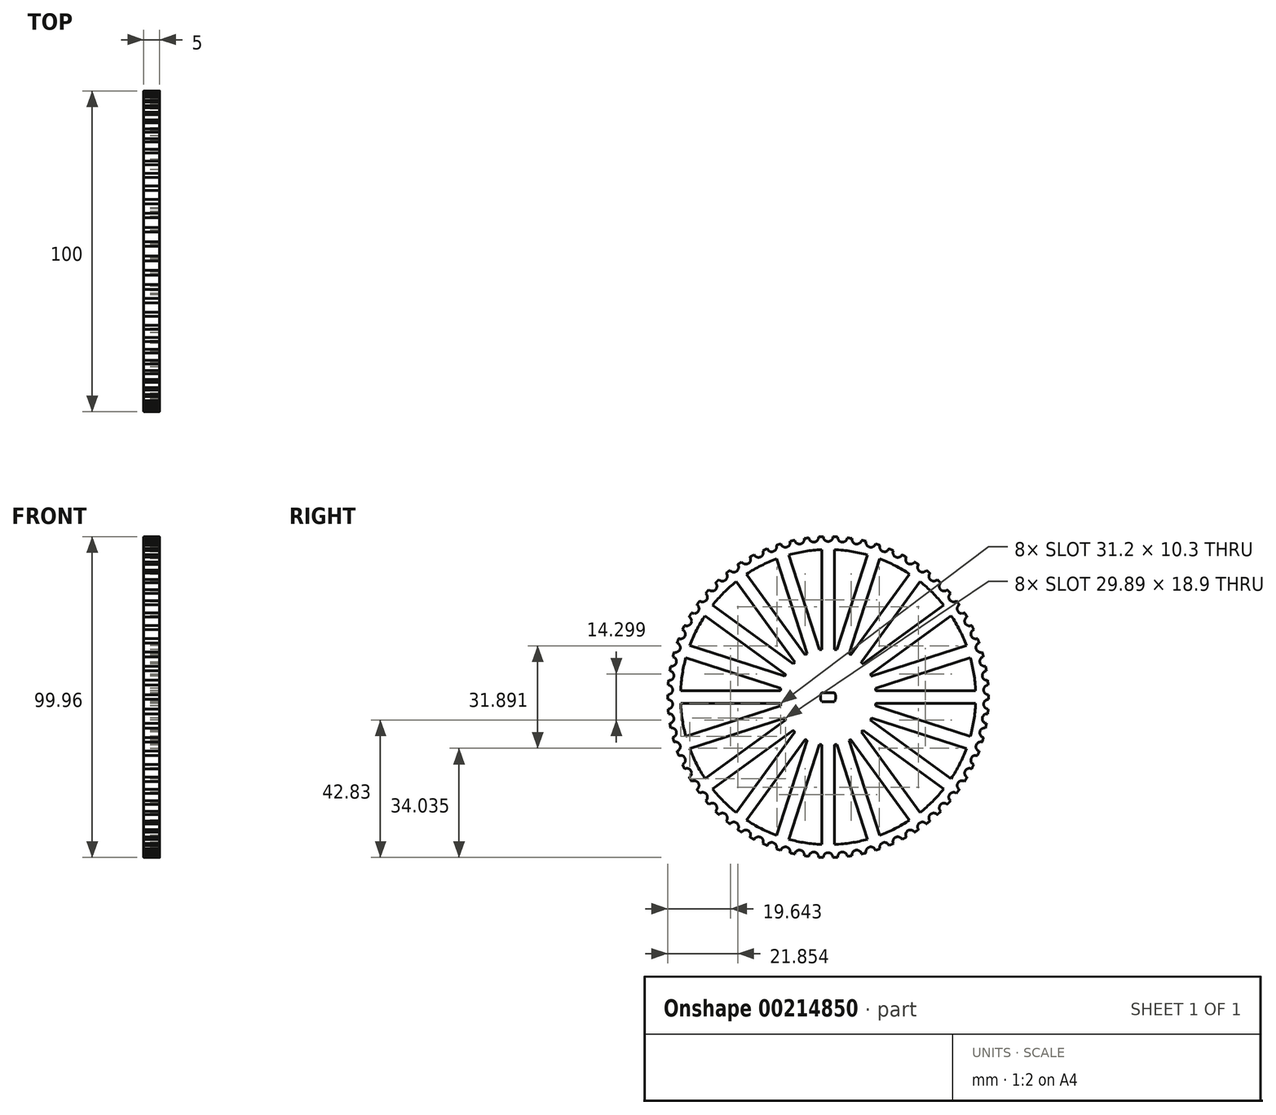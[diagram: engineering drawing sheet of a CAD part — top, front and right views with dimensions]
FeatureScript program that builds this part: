
annotation { "Feature Type Name" : "Feature", "Feature Type Description" : "" }
export const myFeature = defineFeature(function(context is Context, id is Id, definition is map)
    precondition{}
    {
        {
            var Q0;
            Q0=qCreatedBy(makeId("Top.planeOp"),FACE);
            var sketch = newSketch(context, id + "F0", { "sketchPlane" : qUnion([Q0])});
            skLineSegment(sketch, "E0.bottom", {"start": v(-40, 60) * mm, "end": v(40, 60) * mm});
            skLineSegment(sketch, "E0.top", {"start": v(-40, -60) * mm, "end": v(40, -60) * mm});
            skLineSegment(sketch, "E0.left", {"start": v(-40, 60) * mm, "end": v(-40, -60) * mm});
            skLineSegment(sketch, "E0.right", {"start": v(40, 60) * mm, "end": v(40, -60) * mm});
            skPoint(sketch, "E0.middle", {"position": v(0, 0) * mm});
            skSolve(sketch);
        }
        {
            var Q0;
            Q0=sQuery(id+"F0.wireOp",EDGE,"E0.left");
            cPlane(context, id + "F1", {"entities" : qUnion([Q0]), "cplaneType" : CPlaneType.LINE_ANGLE, "offset" : 25 * mm, "angle" : 90 * degree, "width" : 150 * mm, "height" : 150 * mm});
        }
        {
            var Q0;
            Q0=qCreatedBy(id+"F1.planeOp",FACE);
            var sketch = newSketch(context, id + "F2", { "sketchPlane" : qUnion([Q0])});
            skCircle(sketch, "E1", {"center": v(0, 0) * mm, "radius": 50 * mm});
            skCircle(sketch, "E2", {"center": v(0, 0) * mm, "radius": 46 * mm});
            skCircle(sketch, "E3", {"center": v(0, 0) * mm, "radius": 2 * mm});
            skLineSegment(sketch, "E4", {"start": v(0, 2) * mm, "end": v(45.96, 2) * mm});
            skLineSegment(sketch, "E5", {"start": v(0, -2) * mm, "end": v(45.96, -2) * mm});
            skLineSegment(sketch, "E6.1.0", {"start": v(-0.62, 1.9) * mm, "end": v(43.09, 16.1) * mm});
            skLineSegment(sketch, "E6.1.1", {"start": v(0.62, -1.9) * mm, "end": v(44.33, 12.3) * mm});
            skLineSegment(sketch, "E6.2.0", {"start": v(-1.18, 1.62) * mm, "end": v(36, 28.63) * mm});
            skLineSegment(sketch, "E6.2.1", {"start": v(1.18, -1.62) * mm, "end": v(38.36, 25.4) * mm});
            skLineSegment(sketch, "E6.3.0", {"start": v(-1.62, 1.18) * mm, "end": v(25.4, 38.36) * mm});
            skLineSegment(sketch, "E6.3.1", {"start": v(1.62, -1.18) * mm, "end": v(28.63, 36) * mm});
            skLineSegment(sketch, "E6.4.0", {"start": v(-1.9, 0.62) * mm, "end": v(12.3, 44.33) * mm});
            skLineSegment(sketch, "E6.4.1", {"start": v(1.9, -0.62) * mm, "end": v(16.1, 43.09) * mm});
            skLineSegment(sketch, "E6.5.0", {"start": v(-2, 0) * mm, "end": v(-2, 45.96) * mm});
            skLineSegment(sketch, "E6.5.1", {"start": v(2, 0) * mm, "end": v(2, 45.96) * mm});
            skLineSegment(sketch, "E6.6.0", {"start": v(-1.9, -0.62) * mm, "end": v(-16.1, 43.09) * mm});
            skLineSegment(sketch, "E6.6.1", {"start": v(1.9, 0.62) * mm, "end": v(-12.3, 44.33) * mm});
            skLineSegment(sketch, "E6.7.0", {"start": v(-1.62, -1.18) * mm, "end": v(-28.63, 36) * mm});
            skLineSegment(sketch, "E6.7.1", {"start": v(1.62, 1.18) * mm, "end": v(-25.4, 38.36) * mm});
            skLineSegment(sketch, "E6.8.0", {"start": v(-1.18, -1.62) * mm, "end": v(-38.36, 25.4) * mm});
            skLineSegment(sketch, "E6.8.1", {"start": v(1.18, 1.62) * mm, "end": v(-36, 28.63) * mm});
            skLineSegment(sketch, "E6.9.0", {"start": v(-0.62, -1.9) * mm, "end": v(-44.33, 12.3) * mm});
            skLineSegment(sketch, "E6.9.1", {"start": v(0.62, 1.9) * mm, "end": v(-43.09, 16.1) * mm});
            skLineSegment(sketch, "E6.10.0", {"start": v(0, -2) * mm, "end": v(-45.96, -2) * mm});
            skLineSegment(sketch, "E6.10.1", {"start": v(0, 2) * mm, "end": v(-45.96, 2) * mm});
            skLineSegment(sketch, "E6.11.0", {"start": v(0.62, -1.9) * mm, "end": v(-43.09, -16.1) * mm});
            skLineSegment(sketch, "E6.11.1", {"start": v(-0.62, 1.9) * mm, "end": v(-44.33, -12.3) * mm});
            skLineSegment(sketch, "E6.12.0", {"start": v(1.18, -1.62) * mm, "end": v(-36, -28.63) * mm});
            skLineSegment(sketch, "E6.12.1", {"start": v(-1.18, 1.62) * mm, "end": v(-38.36, -25.4) * mm});
            skLineSegment(sketch, "E6.13.0", {"start": v(1.62, -1.18) * mm, "end": v(-25.4, -38.36) * mm});
            skLineSegment(sketch, "E6.13.1", {"start": v(-1.62, 1.18) * mm, "end": v(-28.63, -36) * mm});
            skLineSegment(sketch, "E6.14.0", {"start": v(1.9, -0.62) * mm, "end": v(-12.3, -44.33) * mm});
            skLineSegment(sketch, "E6.14.1", {"start": v(-1.9, 0.62) * mm, "end": v(-16.1, -43.09) * mm});
            skLineSegment(sketch, "E6.15.0", {"start": v(2, 0) * mm, "end": v(2, -45.96) * mm});
            skLineSegment(sketch, "E6.15.1", {"start": v(-2, 0) * mm, "end": v(-2, -45.96) * mm});
            skLineSegment(sketch, "E6.16.0", {"start": v(1.9, 0.62) * mm, "end": v(16.1, -43.09) * mm});
            skLineSegment(sketch, "E6.16.1", {"start": v(-1.9, -0.62) * mm, "end": v(12.3, -44.33) * mm});
            skLineSegment(sketch, "E6.17.0", {"start": v(1.62, 1.18) * mm, "end": v(28.63, -36) * mm});
            skLineSegment(sketch, "E6.17.1", {"start": v(-1.62, -1.18) * mm, "end": v(25.4, -38.36) * mm});
            skLineSegment(sketch, "E6.18.0", {"start": v(1.18, 1.62) * mm, "end": v(38.36, -25.4) * mm});
            skLineSegment(sketch, "E6.18.1", {"start": v(-1.18, -1.62) * mm, "end": v(36, -28.63) * mm});
            skLineSegment(sketch, "E6.19.0", {"start": v(0.62, 1.9) * mm, "end": v(44.33, -12.3) * mm});
            skLineSegment(sketch, "E6.19.1", {"start": v(-0.62, -1.9) * mm, "end": v(43.09, -16.1) * mm});
            skCircle(sketch, "E7", {"center": v(0, 0) * mm, "radius": 12.5 * mm, "construction": true});
            skCircle(sketch, "E8", {"center": v(0, 0) * mm, "radius": 14 * mm});
            skCircle(sketch, "E9", {"center": v(0, 50) * mm, "radius": 1.5 * mm});
            skCircle(sketch, "E10.1.0", {"center": v(-4.48, 49.8) * mm, "radius": 1.5 * mm});
            skCircle(sketch, "E10.2.0", {"center": v(-8.93, 49.2) * mm, "radius": 1.5 * mm});
            skCircle(sketch, "E10.3.0", {"center": v(-13.3, 48.2) * mm, "radius": 1.5 * mm});
            skCircle(sketch, "E10.4.0", {"center": v(-17.57, 46.81) * mm, "radius": 1.5 * mm});
            skCircle(sketch, "E10.5.0", {"center": v(-21.7, 45.05) * mm, "radius": 1.5 * mm});
            skCircle(sketch, "E10.6.0", {"center": v(-25.64, 42.92) * mm, "radius": 1.5 * mm});
            skCircle(sketch, "E10.7.0", {"center": v(-29.39, 40.45) * mm, "radius": 1.5 * mm});
            skCircle(sketch, "E10.8.0", {"center": v(-32.9, 37.65) * mm, "radius": 1.5 * mm});
            skCircle(sketch, "E10.9.0", {"center": v(-36.14, 34.55) * mm, "radius": 1.5 * mm});
            skCircle(sketch, "E10.10.0", {"center": v(-39.1, 31.17) * mm, "radius": 1.5 * mm});
            skCircle(sketch, "E10.11.0", {"center": v(-41.73, 27.54) * mm, "radius": 1.5 * mm});
            skCircle(sketch, "E10.12.0", {"center": v(-44.03, 23.7) * mm, "radius": 1.5 * mm});
            skCircle(sketch, "E10.13.0", {"center": v(-45.98, 19.65) * mm, "radius": 1.5 * mm});
            skCircle(sketch, "E10.14.0", {"center": v(-47.55, 15.45) * mm, "radius": 1.5 * mm});
            skCircle(sketch, "E10.15.0", {"center": v(-48.75, 11.13) * mm, "radius": 1.5 * mm});
            skCircle(sketch, "E10.16.0", {"center": v(-49.55, 6.71) * mm, "radius": 1.5 * mm});
            skCircle(sketch, "E10.17.0", {"center": v(-49.95, 2.24) * mm, "radius": 1.5 * mm});
            skCircle(sketch, "E10.18.0", {"center": v(-49.95, -2.24) * mm, "radius": 1.5 * mm});
            skCircle(sketch, "E10.19.0", {"center": v(-49.55, -6.71) * mm, "radius": 1.5 * mm});
            skCircle(sketch, "E10.20.0", {"center": v(-48.75, -11.13) * mm, "radius": 1.5 * mm});
            skCircle(sketch, "E10.21.0", {"center": v(-47.55, -15.45) * mm, "radius": 1.5 * mm});
            skCircle(sketch, "E10.22.0", {"center": v(-45.98, -19.65) * mm, "radius": 1.5 * mm});
            skCircle(sketch, "E10.23.0", {"center": v(-44.03, -23.7) * mm, "radius": 1.5 * mm});
            skCircle(sketch, "E10.24.0", {"center": v(-41.73, -27.54) * mm, "radius": 1.5 * mm});
            skCircle(sketch, "E10.25.0", {"center": v(-39.1, -31.17) * mm, "radius": 1.5 * mm});
            skCircle(sketch, "E10.26.0", {"center": v(-36.14, -34.55) * mm, "radius": 1.5 * mm});
            skCircle(sketch, "E10.27.0", {"center": v(-32.9, -37.65) * mm, "radius": 1.5 * mm});
            skCircle(sketch, "E10.28.0", {"center": v(-29.39, -40.45) * mm, "radius": 1.5 * mm});
            skCircle(sketch, "E10.29.0", {"center": v(-25.64, -42.92) * mm, "radius": 1.5 * mm});
            skCircle(sketch, "E10.30.0", {"center": v(-21.7, -45.05) * mm, "radius": 1.5 * mm});
            skCircle(sketch, "E10.31.0", {"center": v(-17.57, -46.81) * mm, "radius": 1.5 * mm});
            skCircle(sketch, "E10.32.0", {"center": v(-13.3, -48.2) * mm, "radius": 1.5 * mm});
            skCircle(sketch, "E10.33.0", {"center": v(-8.93, -49.2) * mm, "radius": 1.5 * mm});
            skCircle(sketch, "E10.34.0", {"center": v(-4.48, -49.8) * mm, "radius": 1.5 * mm});
            skCircle(sketch, "E10.35.0", {"center": v(0, -50) * mm, "radius": 1.5 * mm});
            skCircle(sketch, "E10.36.0", {"center": v(4.48, -49.8) * mm, "radius": 1.5 * mm});
            skCircle(sketch, "E10.37.0", {"center": v(8.93, -49.2) * mm, "radius": 1.5 * mm});
            skCircle(sketch, "E10.38.0", {"center": v(13.3, -48.2) * mm, "radius": 1.5 * mm});
            skCircle(sketch, "E10.39.0", {"center": v(17.57, -46.81) * mm, "radius": 1.5 * mm});
            skCircle(sketch, "E10.40.0", {"center": v(21.7, -45.05) * mm, "radius": 1.5 * mm});
            skCircle(sketch, "E10.41.0", {"center": v(25.64, -42.92) * mm, "radius": 1.5 * mm});
            skCircle(sketch, "E10.42.0", {"center": v(29.39, -40.45) * mm, "radius": 1.5 * mm});
            skCircle(sketch, "E10.43.0", {"center": v(32.9, -37.65) * mm, "radius": 1.5 * mm});
            skCircle(sketch, "E10.44.0", {"center": v(36.14, -34.55) * mm, "radius": 1.5 * mm});
            skCircle(sketch, "E10.45.0", {"center": v(39.1, -31.17) * mm, "radius": 1.5 * mm});
            skCircle(sketch, "E10.46.0", {"center": v(41.73, -27.54) * mm, "radius": 1.5 * mm});
            skCircle(sketch, "E10.47.0", {"center": v(44.03, -23.7) * mm, "radius": 1.5 * mm});
            skCircle(sketch, "E10.48.0", {"center": v(45.98, -19.65) * mm, "radius": 1.5 * mm});
            skCircle(sketch, "E10.49.0", {"center": v(47.55, -15.45) * mm, "radius": 1.5 * mm});
            skCircle(sketch, "E10.50.0", {"center": v(48.75, -11.13) * mm, "radius": 1.5 * mm});
            skCircle(sketch, "E10.51.0", {"center": v(49.55, -6.71) * mm, "radius": 1.5 * mm});
            skCircle(sketch, "E10.52.0", {"center": v(49.95, -2.24) * mm, "radius": 1.5 * mm});
            skCircle(sketch, "E10.53.0", {"center": v(49.95, 2.24) * mm, "radius": 1.5 * mm});
            skCircle(sketch, "E10.54.0", {"center": v(49.55, 6.71) * mm, "radius": 1.5 * mm});
            skCircle(sketch, "E10.55.0", {"center": v(48.75, 11.13) * mm, "radius": 1.5 * mm});
            skCircle(sketch, "E10.56.0", {"center": v(47.55, 15.45) * mm, "radius": 1.5 * mm});
            skCircle(sketch, "E10.57.0", {"center": v(45.98, 19.65) * mm, "radius": 1.5 * mm});
            skCircle(sketch, "E10.58.0", {"center": v(44.03, 23.7) * mm, "radius": 1.5 * mm});
            skCircle(sketch, "E10.59.0", {"center": v(41.73, 27.54) * mm, "radius": 1.5 * mm});
            skCircle(sketch, "E10.60.0", {"center": v(39.1, 31.17) * mm, "radius": 1.5 * mm});
            skCircle(sketch, "E10.61.0", {"center": v(36.14, 34.55) * mm, "radius": 1.5 * mm});
            skCircle(sketch, "E10.62.0", {"center": v(32.9, 37.65) * mm, "radius": 1.5 * mm});
            skCircle(sketch, "E10.63.0", {"center": v(29.39, 40.45) * mm, "radius": 1.5 * mm});
            skCircle(sketch, "E10.64.0", {"center": v(25.64, 42.92) * mm, "radius": 1.5 * mm});
            skCircle(sketch, "E10.65.0", {"center": v(21.7, 45.05) * mm, "radius": 1.5 * mm});
            skCircle(sketch, "E10.66.0", {"center": v(17.57, 46.81) * mm, "radius": 1.5 * mm});
            skCircle(sketch, "E10.67.0", {"center": v(13.3, 48.2) * mm, "radius": 1.5 * mm});
            skCircle(sketch, "E10.68.0", {"center": v(8.93, 49.2) * mm, "radius": 1.5 * mm});
            skCircle(sketch, "E10.69.0", {"center": v(4.48, 49.8) * mm, "radius": 1.5 * mm});
            skSolve(sketch);
        }
        {
            var Q0;
            Q0=qCreatedBy(id+"F1.planeOp",FACE);
            var sketch = newSketch(context, id + "F3", { "sketchPlane" : qUnion([Q0])});
            skCircle(sketch, "E11", {"center": v(0, 0) * mm, "radius": 15 * mm});
            skCircle(sketch, "E12.0", {"center": v(0, 0) * mm, "radius": 46 * mm});
            skCircle(sketch, "E13.0", {"center": v(0, 0) * mm, "radius": 50 * mm});
            skCircle(sketch, "E14", {"center": v(0, 0) * mm, "radius": 2.4 * mm});
            skLineSegment(sketch, "E15", {"start": v(1.95, 1.4) * mm, "end": v(-1.95, 1.4) * mm});
            skLineSegment(sketch, "E16.MirrorCS", {"start": v(1.95, -1.4) * mm, "end": v(-1.95, -1.4) * mm});
            skSolve(sketch);
        }
        {
            var Q0;
            Q0=makeQuery(id+"F3.imprint","IMPRINT",FACE,{"disambiguationData":[TD([[makeQuery(id+"F3.imprint","IMPRINT",EDGE,{"derivedFrom":sQuery(id+"F3.wireOp",EDGE,"E11")}),1.0]])]});
            var Q1;
            {var subQ0=sQuery(id+"F3.wireOp",EDGE,"E15");Q1=makeQuery(id+"F3.imprint","IMPRINT",FACE,{"disambiguationData":[TD([[makeQuery(id+"F3.imprint","IMPRINT",EDGE,{"derivedFrom":subQ0}),-1.0]])]});}
            var Q2;
            {var subQ0=sQuery(id+"F3.wireOp",EDGE,"E16.MirrorCS");Q2=makeQuery(id+"F3.imprint","IMPRINT",FACE,{"disambiguationData":[TD([[makeQuery(id+"F3.imprint","IMPRINT",EDGE,{"derivedFrom":subQ0}),1.0]])]});}
            extrude(context, id + "F4", {"entities" : qUnion([Q0, Q1, Q2]), "depth" : 5 * mm});
        }
        {
            var Q0;
            {var subQ0=sQuery(id+"F2.wireOp",EDGE,"E6.3.0");var subQ1=sQuery(id+"F2.wireOp",EDGE,"E2");var subQ2=makeQuery(id+"F2.imprint","INTERSECT",VERTEX,{"derivedFrom":[subQ1,subQ0]});Q0=makeQuery(id+"F2.imprint","IMPRINT",FACE,{"disambiguationData":[TD([[makeQuery(id+"F2.imprint","IMPRINT",EDGE,{"disambiguationData":[TD([[subQ2,1.0]])],"derivedFrom":subQ1}),1.0]])]});}
            var Q1;
            {var subQ0=sQuery(id+"F2.wireOp",EDGE,"E6.2.0");var subQ1=sQuery(id+"F2.wireOp",EDGE,"E2");var subQ2=makeQuery(id+"F2.imprint","INTERSECT",VERTEX,{"derivedFrom":[subQ1,subQ0]});Q1=makeQuery(id+"F2.imprint","IMPRINT",FACE,{"disambiguationData":[TD([[makeQuery(id+"F2.imprint","IMPRINT",EDGE,{"disambiguationData":[TD([[subQ2,1.0]])],"derivedFrom":subQ1}),1.0]])]});}
            var Q2;
            {var subQ0=sQuery(id+"F2.wireOp",EDGE,"E6.1.0");var subQ1=sQuery(id+"F2.wireOp",EDGE,"E2");var subQ2=makeQuery(id+"F2.imprint","INTERSECT",VERTEX,{"derivedFrom":[subQ1,subQ0]});Q2=makeQuery(id+"F2.imprint","IMPRINT",FACE,{"disambiguationData":[TD([[makeQuery(id+"F2.imprint","IMPRINT",EDGE,{"disambiguationData":[TD([[subQ2,1.0]])],"derivedFrom":subQ1}),1.0]])]});}
            var Q3;
            {var subQ0=sQuery(id+"F2.wireOp",EDGE,"E4");var subQ1=sQuery(id+"F2.wireOp",EDGE,"E2");var subQ2=makeQuery(id+"F2.imprint","INTERSECT",VERTEX,{"derivedFrom":[subQ1,subQ0]});Q3=makeQuery(id+"F2.imprint","IMPRINT",FACE,{"disambiguationData":[TD([[makeQuery(id+"F2.imprint","IMPRINT",EDGE,{"disambiguationData":[TD([[subQ2,1.0]])],"derivedFrom":subQ1}),1.0]])]});}
            var Q4;
            {var subQ0=sQuery(id+"F2.wireOp",EDGE,"E6.19.0");var subQ1=sQuery(id+"F2.wireOp",EDGE,"E2");var subQ2=makeQuery(id+"F2.imprint","INTERSECT",VERTEX,{"derivedFrom":[subQ1,subQ0]});Q4=makeQuery(id+"F2.imprint","IMPRINT",FACE,{"disambiguationData":[TD([[makeQuery(id+"F2.imprint","IMPRINT",EDGE,{"disambiguationData":[TD([[subQ2,1.0]])],"derivedFrom":subQ1}),1.0]])]});}
            var Q5;
            {var subQ0=sQuery(id+"F2.wireOp",EDGE,"E6.18.0");var subQ1=sQuery(id+"F2.wireOp",EDGE,"E2");var subQ2=makeQuery(id+"F2.imprint","INTERSECT",VERTEX,{"derivedFrom":[subQ1,subQ0]});Q5=makeQuery(id+"F2.imprint","IMPRINT",FACE,{"disambiguationData":[TD([[makeQuery(id+"F2.imprint","IMPRINT",EDGE,{"disambiguationData":[TD([[subQ2,1.0]])],"derivedFrom":subQ1}),1.0]])]});}
            var Q6;
            {var subQ0=sQuery(id+"F2.wireOp",EDGE,"E6.17.0");var subQ1=sQuery(id+"F2.wireOp",EDGE,"E2");var subQ2=makeQuery(id+"F2.imprint","INTERSECT",VERTEX,{"derivedFrom":[subQ1,subQ0]});Q6=makeQuery(id+"F2.imprint","IMPRINT",FACE,{"disambiguationData":[TD([[makeQuery(id+"F2.imprint","IMPRINT",EDGE,{"disambiguationData":[TD([[subQ2,1.0]])],"derivedFrom":subQ1}),1.0]])]});}
            var Q7;
            {var subQ0=sQuery(id+"F2.wireOp",EDGE,"E6.16.0");var subQ1=sQuery(id+"F2.wireOp",EDGE,"E2");var subQ2=makeQuery(id+"F2.imprint","INTERSECT",VERTEX,{"derivedFrom":[subQ1,subQ0]});Q7=makeQuery(id+"F2.imprint","IMPRINT",FACE,{"disambiguationData":[TD([[makeQuery(id+"F2.imprint","IMPRINT",EDGE,{"disambiguationData":[TD([[subQ2,1.0]])],"derivedFrom":subQ1}),1.0]])]});}
            var Q8;
            {var subQ0=sQuery(id+"F2.wireOp",EDGE,"E6.15.0");var subQ1=sQuery(id+"F2.wireOp",EDGE,"E2");var subQ2=makeQuery(id+"F2.imprint","INTERSECT",VERTEX,{"derivedFrom":[subQ1,subQ0]});Q8=makeQuery(id+"F2.imprint","IMPRINT",FACE,{"disambiguationData":[TD([[makeQuery(id+"F2.imprint","IMPRINT",EDGE,{"disambiguationData":[TD([[subQ2,1.0]])],"derivedFrom":subQ1}),1.0]])]});}
            var Q9;
            {var subQ0=sQuery(id+"F2.wireOp",EDGE,"E6.14.0");var subQ1=sQuery(id+"F2.wireOp",EDGE,"E2");var subQ2=makeQuery(id+"F2.imprint","INTERSECT",VERTEX,{"derivedFrom":[subQ1,subQ0]});Q9=makeQuery(id+"F2.imprint","IMPRINT",FACE,{"disambiguationData":[TD([[makeQuery(id+"F2.imprint","IMPRINT",EDGE,{"disambiguationData":[TD([[subQ2,1.0]])],"derivedFrom":subQ1}),1.0]])]});}
            var Q10;
            {var subQ0=sQuery(id+"F2.wireOp",EDGE,"E6.13.0");var subQ1=sQuery(id+"F2.wireOp",EDGE,"E2");var subQ2=makeQuery(id+"F2.imprint","INTERSECT",VERTEX,{"derivedFrom":[subQ1,subQ0]});Q10=makeQuery(id+"F2.imprint","IMPRINT",FACE,{"disambiguationData":[TD([[makeQuery(id+"F2.imprint","IMPRINT",EDGE,{"disambiguationData":[TD([[subQ2,1.0]])],"derivedFrom":subQ1}),1.0]])]});}
            var Q11;
            {var subQ0=sQuery(id+"F2.wireOp",EDGE,"E6.12.0");var subQ1=sQuery(id+"F2.wireOp",EDGE,"E2");var subQ2=makeQuery(id+"F2.imprint","INTERSECT",VERTEX,{"derivedFrom":[subQ1,subQ0]});Q11=makeQuery(id+"F2.imprint","IMPRINT",FACE,{"disambiguationData":[TD([[makeQuery(id+"F2.imprint","IMPRINT",EDGE,{"disambiguationData":[TD([[subQ2,1.0]])],"derivedFrom":subQ1}),1.0]])]});}
            var Q12;
            {var subQ0=sQuery(id+"F2.wireOp",EDGE,"E6.11.0");var subQ1=sQuery(id+"F2.wireOp",EDGE,"E2");var subQ2=makeQuery(id+"F2.imprint","INTERSECT",VERTEX,{"derivedFrom":[subQ1,subQ0]});Q12=makeQuery(id+"F2.imprint","IMPRINT",FACE,{"disambiguationData":[TD([[makeQuery(id+"F2.imprint","IMPRINT",EDGE,{"disambiguationData":[TD([[subQ2,1.0]])],"derivedFrom":subQ1}),1.0]])]});}
            var Q13;
            {var subQ0=sQuery(id+"F2.wireOp",EDGE,"E6.9.0");var subQ1=sQuery(id+"F2.wireOp",EDGE,"E2");var subQ2=makeQuery(id+"F2.imprint","INTERSECT",VERTEX,{"derivedFrom":[subQ1,subQ0]});Q13=makeQuery(id+"F2.imprint","IMPRINT",FACE,{"disambiguationData":[TD([[makeQuery(id+"F2.imprint","IMPRINT",EDGE,{"disambiguationData":[TD([[subQ2,1.0]])],"derivedFrom":subQ1}),1.0]])]});}
            var Q14;
            {var subQ0=sQuery(id+"F2.wireOp",EDGE,"E6.10.0");var subQ1=sQuery(id+"F2.wireOp",EDGE,"E2");var subQ2=makeQuery(id+"F2.imprint","INTERSECT",VERTEX,{"derivedFrom":[subQ1,subQ0]});Q14=makeQuery(id+"F2.imprint","IMPRINT",FACE,{"disambiguationData":[TD([[makeQuery(id+"F2.imprint","IMPRINT",EDGE,{"disambiguationData":[TD([[subQ2,1.0]])],"derivedFrom":subQ1}),1.0]])]});}
            var Q15;
            {var subQ0=sQuery(id+"F2.wireOp",EDGE,"E6.8.0");var subQ1=sQuery(id+"F2.wireOp",EDGE,"E2");var subQ2=makeQuery(id+"F2.imprint","INTERSECT",VERTEX,{"derivedFrom":[subQ1,subQ0]});Q15=makeQuery(id+"F2.imprint","IMPRINT",FACE,{"disambiguationData":[TD([[makeQuery(id+"F2.imprint","IMPRINT",EDGE,{"disambiguationData":[TD([[subQ2,1.0]])],"derivedFrom":subQ1}),1.0]])]});}
            var Q16;
            {var subQ0=sQuery(id+"F2.wireOp",EDGE,"E6.7.0");var subQ1=sQuery(id+"F2.wireOp",EDGE,"E2");var subQ2=makeQuery(id+"F2.imprint","INTERSECT",VERTEX,{"derivedFrom":[subQ1,subQ0]});Q16=makeQuery(id+"F2.imprint","IMPRINT",FACE,{"disambiguationData":[TD([[makeQuery(id+"F2.imprint","IMPRINT",EDGE,{"disambiguationData":[TD([[subQ2,1.0]])],"derivedFrom":subQ1}),1.0]])]});}
            var Q17;
            {var subQ0=sQuery(id+"F2.wireOp",EDGE,"E6.6.0");var subQ1=sQuery(id+"F2.wireOp",EDGE,"E2");var subQ2=makeQuery(id+"F2.imprint","INTERSECT",VERTEX,{"derivedFrom":[subQ1,subQ0]});Q17=makeQuery(id+"F2.imprint","IMPRINT",FACE,{"disambiguationData":[TD([[makeQuery(id+"F2.imprint","IMPRINT",EDGE,{"disambiguationData":[TD([[subQ2,1.0]])],"derivedFrom":subQ1}),1.0]])]});}
            var Q18;
            {var subQ0=sQuery(id+"F2.wireOp",EDGE,"E6.5.0");var subQ1=sQuery(id+"F2.wireOp",EDGE,"E2");var subQ2=makeQuery(id+"F2.imprint","INTERSECT",VERTEX,{"derivedFrom":[subQ1,subQ0]});Q18=makeQuery(id+"F2.imprint","IMPRINT",FACE,{"disambiguationData":[TD([[makeQuery(id+"F2.imprint","IMPRINT",EDGE,{"disambiguationData":[TD([[subQ2,1.0]])],"derivedFrom":subQ1}),1.0]])]});}
            var Q19;
            {var subQ0=sQuery(id+"F2.wireOp",EDGE,"E6.4.0");var subQ1=sQuery(id+"F2.wireOp",EDGE,"E2");var subQ2=makeQuery(id+"F2.imprint","INTERSECT",VERTEX,{"derivedFrom":[subQ1,subQ0]});Q19=makeQuery(id+"F2.imprint","IMPRINT",FACE,{"disambiguationData":[TD([[makeQuery(id+"F2.imprint","IMPRINT",EDGE,{"disambiguationData":[TD([[subQ2,1.0]])],"derivedFrom":subQ1}),1.0]])]});}
            extrude(context, id + "F5", {"entities" : qUnion([Q0, Q1, Q2, Q3, Q4, Q5, Q6, Q7, Q8, Q9, Q10, Q11, Q12, Q13, Q14, Q15, Q16, Q17, Q18, Q19]), "operationType" : NewBodyOperationType.ADD, "depth" : 5 * mm});
        }
        {
            var Q0;
            Q0=makeQuery(id+"F2.imprint","IMPRINT",FACE,{"disambiguationData":[TD([[makeQuery(id+"F2.imprint","IMPRINT",EDGE,{"derivedFrom":sQuery(id+"F2.wireOp",EDGE,"E1")}),1.0]])]});
            extrude(context, id + "F6", {"entities" : qUnion([Q0]), "operationType" : NewBodyOperationType.ADD, "depth" : 5 * mm});
        }
    });
